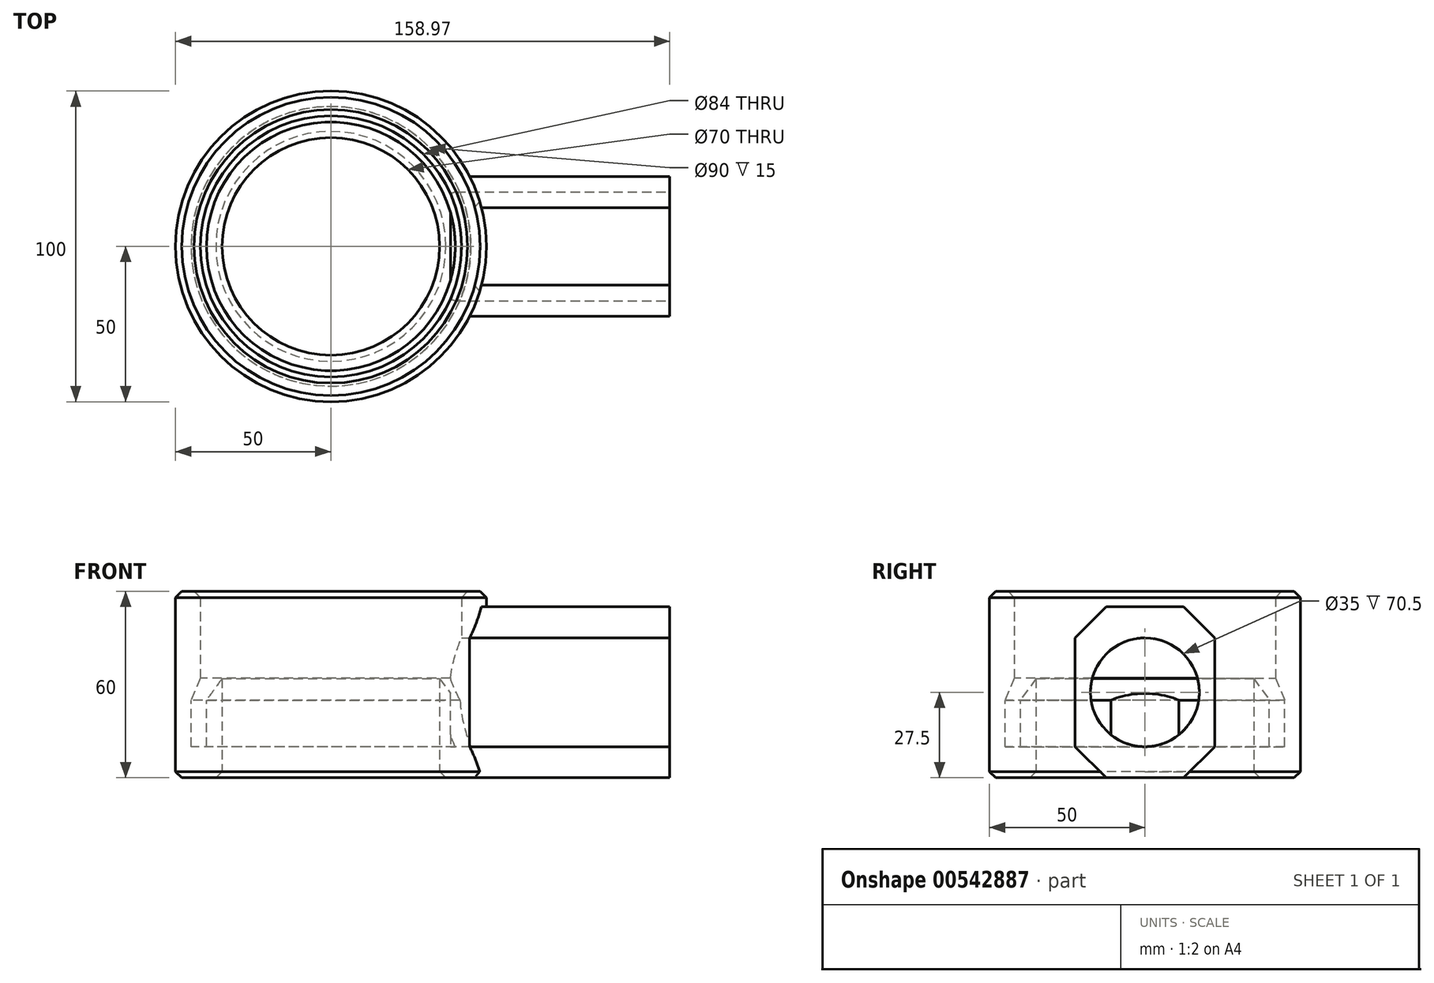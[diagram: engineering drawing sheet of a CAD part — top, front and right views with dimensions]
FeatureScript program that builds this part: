
annotation { "Feature Type Name" : "Feature", "Feature Type Description" : "" }
export const myFeature = defineFeature(function(context is Context, id is Id, definition is map)
    precondition{}
    {
        {
            var Q0;
            Q0=qCreatedBy(makeId("Front.planeOp"),FACE);
            var sketch = newSketch(context, id + "F0", { "sketchPlane" : qUnion([Q0])});
            skLineSegment(sketch, "E0", {"start": v(0, 0) * mm, "end": v(0, 37.27) * mm, "construction": true});
            skLineSegment(sketch, "E1", {"start": v(0, 0) * mm, "end": v(35, 0) * mm, "construction": true});
            skLineSegment(sketch, "E2", {"start": v(35, 0) * mm, "end": v(35, 32) * mm});
            skLineSegment(sketch, "E3", {"start": v(35, 32) * mm, "end": v(42, 32) * mm});
            skLineSegment(sketch, "E4", {"start": v(42, 32) * mm, "end": v(42, 60) * mm});
            skLineSegment(sketch, "E5", {"start": v(42, 60) * mm, "end": v(50, 60) * mm});
            skLineSegment(sketch, "E6", {"start": v(50, 60) * mm, "end": v(50, 0) * mm});
            skLineSegment(sketch, "E7", {"start": v(50, 0) * mm, "end": v(35, 0) * mm});
            skSolve(sketch);
        }
        {
            var Q0;
            Q0=makeQuery(id+"F0.imprint","IMPRINT",FACE,{"disambiguationData":[TD([[makeQuery(id+"F0.imprint","IMPRINT",EDGE,{"derivedFrom":sQuery(id+"F0.wireOp",EDGE,"E2")}),-1.0]])]});
            var Q1;
            Q1=sQuery(id+"F0.wireOp",EDGE,"E0");
            revolve(context, id + "F1", {"entities" : qUnion([Q0]), "axis" : qUnion([Q1]), "revolveType" : RevolveType.FULL});
        }
        {
            var Q0;
            Q0=qCreatedBy(makeId("Front.planeOp"),FACE);
            var sketch = newSketch(context, id + "F2", { "sketchPlane" : qUnion([Q0])});
            skLineSegment(sketch, "E8", {"start": v(35, 0) * mm, "end": v(35, 10) * mm, "construction": true});
            skLineSegment(sketch, "E9", {"start": v(35, 10) * mm, "end": v(35, 25) * mm, "construction": true});
            skLineSegment(sketch, "E10", {"start": v(35, 10) * mm, "end": v(40, 10) * mm, "construction": true});
            skLineSegment(sketch, "E11", {"start": v(35, 25) * mm, "end": v(40, 25) * mm, "construction": true});
            skLineSegment(sketch, "E12", {"start": v(40, 25) * mm, "end": v(40, 10) * mm});
            skLineSegment(sketch, "E13", {"start": v(40, 25) * mm, "end": v(34.96, 32) * mm});
            skLineSegment(sketch, "E14", {"start": v(40, 10) * mm, "end": v(45, 10) * mm});
            skLineSegment(sketch, "E15", {"start": v(45, 10) * mm, "end": v(45, 25) * mm});
            skLineSegment(sketch, "E16", {"start": v(45, 25) * mm, "end": v(39.9, 37) * mm});
            skLineSegment(sketch, "E17", {"start": v(39.9, 37) * mm, "end": v(34.96, 32) * mm});
            skLineSegment(sketch, "E18", {"start": v(0, 0) * mm, "end": v(0, 25.1) * mm, "construction": true});
            skSolve(sketch);
        }
        {
            var Q0;
            Q0 = qSketchRegion(id + "F2", true);
            var Q1;
            Q1=sQuery(id+"F2.wireOp",EDGE,"E18");
            revolve(context, id + "F3", {"operationType" : NewBodyOperationType.REMOVE, "entities" : qUnion([Q0]), "axis" : qUnion([Q1]), "revolveType" : RevolveType.FULL, "oppositeDirection" : true});
        }
        {
            var Q0;
            Q0=qCreatedBy(makeId("Top.planeOp"),FACE);
            var sketch = newSketch(context, id + "F4", { "sketchPlane" : qUnion([Q0])});
            skArc(sketch, "E19", {"start": v(48.5, 0) * mm, "mid": v(47.1, 11.59) * mm, "end": v(42.97, 22.5) * mm});
            skArc(sketch, "E20", {"start": v(48.5, 0) * mm, "mid": v(47.1, -11.59) * mm, "end": v(42.97, -22.5) * mm});
            skLineSegment(sketch, "E21", {"start": v(42.97, 22.5) * mm, "end": v(108.97, 22.5) * mm});
            skLineSegment(sketch, "E22", {"start": v(42.97, -22.5) * mm, "end": v(108.97, -22.5) * mm});
            skLineSegment(sketch, "E23", {"start": v(108.97, 22.5) * mm, "end": v(108.97, -22.5) * mm});
            skSolve(sketch);
        }
        {
            var Q0;
            Q0=makeQuery(id+"F4.imprint","IMPRINT",FACE,{"disambiguationData":[TD([[makeQuery(id+"F4.imprint","IMPRINT",EDGE,{"derivedFrom":sQuery(id+"F4.wireOp",EDGE,"E19")}),-1.0]])]});
            extrude(context, id + "F5", {"entities" : qUnion([Q0]), "operationType" : NewBodyOperationType.ADD, "depth" : 55 * mm, "offsetDistance" : 25 * mm});
        }
        {
            var Q0;
            Q0=makeQuery(id+"F5.opExtrude","SWEPT_FACE",FACE,{"disambiguationData":[OSD([sQuery(id+"F4.wireOp",EDGE,"E23")])]});
            var sketch = newSketch(context, id + "F6", { "sketchPlane" : qUnion([Q0])});
            skLineSegment(sketch, "E24", {"start": v(0, 0) * mm, "end": v(0, 10) * mm, "construction": true});
            skPoint(sketch, "E24.endSnap0", {"position": v(0, 0) * mm});
            skLineSegment(sketch, "E25", {"start": v(0, 10) * mm, "end": v(0, 27.5) * mm, "construction": true});
            skCircle(sketch, "E26", {"center": v(0, 27.5) * mm, "radius": 17.5 * mm});
            skSolve(sketch);
        }
        {
            var Q0;
            Q0=makeQuery(id+"F6.imprint","IMPRINT",FACE,{"disambiguationData":[TD([[makeQuery(id+"F6.imprint","IMPRINT",EDGE,{"derivedFrom":sQuery(id+"F6.wireOp",EDGE,"E26")}),1.0]])]});
            extrude(context, id + "F7", {"entities" : qUnion([Q0]), "operationType" : NewBodyOperationType.REMOVE, "oppositeDirection" : true, "depth" : 70.5 * mm, "offsetDistance" : 25 * mm});
        }
        {
            var Q0;
            Q0=makeQuery(id+"F5.opExtrude","CAP_EDGE",EDGE,{"disambiguationData":[OSD([sQuery(id+"F4.wireOp",EDGE,"E22")])],"isStart":false});
            var Q1;
            Q1=makeQuery(id+"F5.opExtrude","CAP_EDGE",EDGE,{"disambiguationData":[OSD([sQuery(id+"F4.wireOp",EDGE,"E22")])],"isStart":true});
            var Q2;
            Q2=makeQuery(id+"F5.opExtrude","CAP_EDGE",EDGE,{"disambiguationData":[OSD([sQuery(id+"F4.wireOp",EDGE,"E21")])],"isStart":false});
            var Q3;
            Q3=makeQuery(id+"F5.opExtrude","CAP_EDGE",EDGE,{"disambiguationData":[OSD([sQuery(id+"F4.wireOp",EDGE,"E21")])],"isStart":true});
            chamfer(context, id + "F8", {"entities" : qUnion([Q0, Q1, Q2, Q3]), "width" : 10 * mm, "tangentPropagation" : true});
        }
        {
            var Q0;
            Q0=makeQuery(id+"F1.opRevolve","SWEPT_EDGE",EDGE,{"disambiguationData":[OSD([sQuery(id+"F0.wireOp",EDGE,"E5"),sQuery(id+"F0.wireOp",EDGE,"E6")])]});
            var Q1;
            Q1=makeQuery(id+"F1.opRevolve","SWEPT_EDGE",EDGE,{"disambiguationData":[OSD([sQuery(id+"F0.wireOp",EDGE,"E4"),sQuery(id+"F0.wireOp",EDGE,"E5")])]});
            var Q2;
            Q2=makeQuery(id+"F1.opRevolve","SWEPT_EDGE",EDGE,{"disambiguationData":[OSD([sQuery(id+"F0.wireOp",EDGE,"E2"),sQuery(id+"F0.wireOp",EDGE,"E7")])]});
            var Q3;
            Q3=makeQuery(id+"F1.opRevolve","SWEPT_EDGE",EDGE,{"disambiguationData":[OSD([sQuery(id+"F0.wireOp",EDGE,"E6"),sQuery(id+"F0.wireOp",EDGE,"E7")])]});
            chamfer(context, id + "F9", {"entities" : qUnion([Q0, Q1, Q2, Q3]), "width" : 2 * mm, "tangentPropagation" : true});
        }
    });
